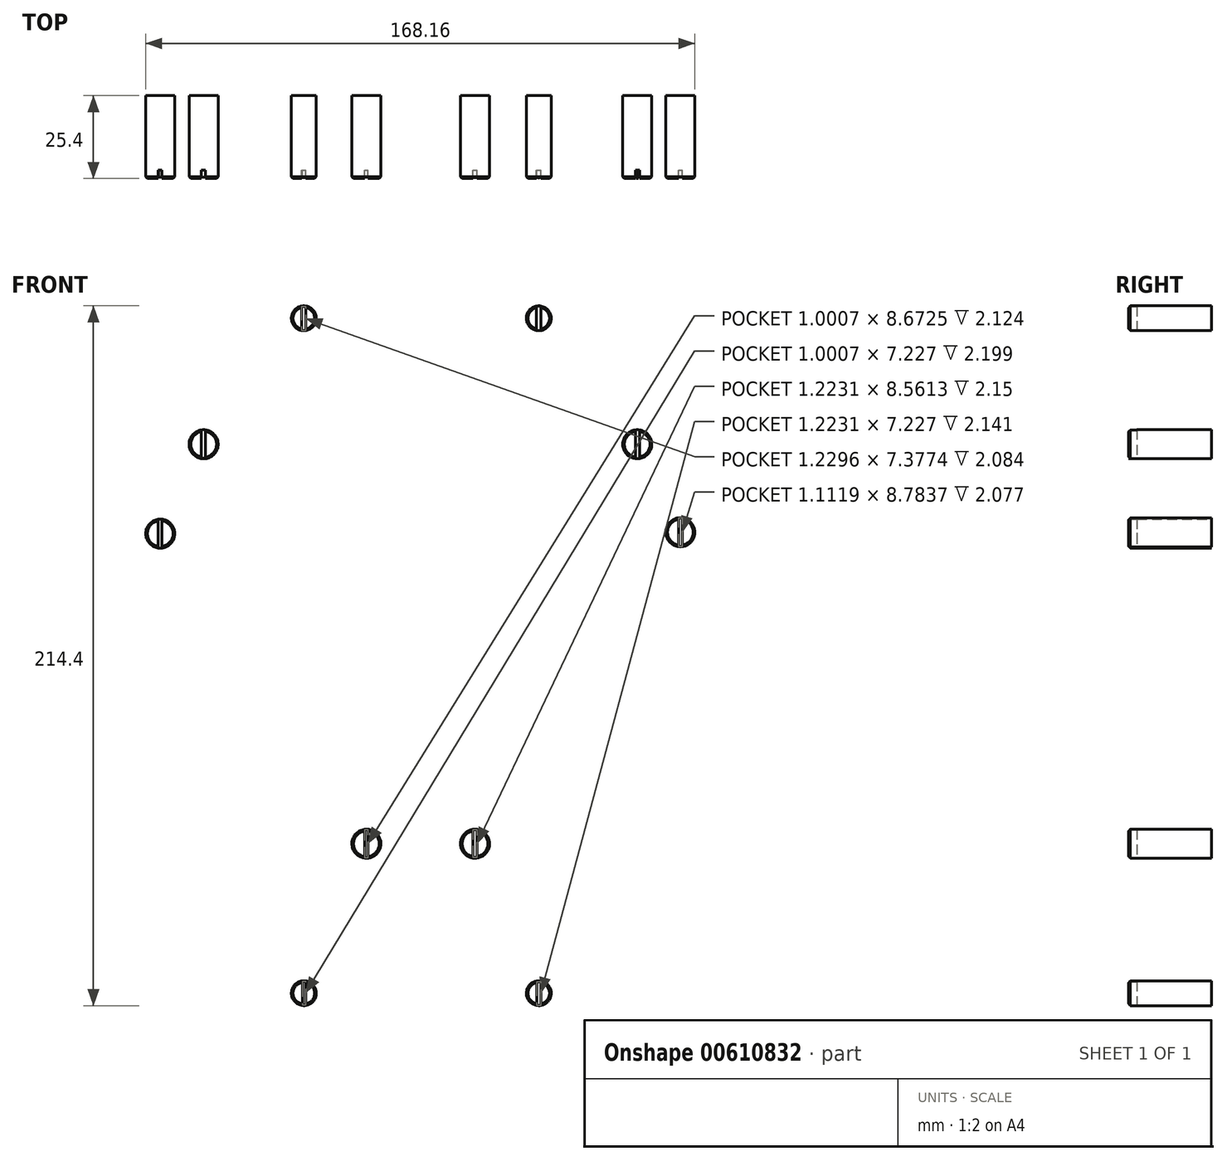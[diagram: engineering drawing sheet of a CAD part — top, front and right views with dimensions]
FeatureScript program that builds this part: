
annotation { "Feature Type Name" : "Feature", "Feature Type Description" : "" }
export const myFeature = defineFeature(function(context is Context, id is Id, definition is map)
    precondition{}
    {
        {
            var Q0;
            Q0=qCreatedBy(makeId("Front.planeOp"),FACE);
            var sketch = newSketch(context, id + "F0", { "sketchPlane" : qUnion([Q0])});
            skCircle(sketch, "E0", {"center": v(-35.62, -111.7) * mm, "radius": 3.81 * mm});
            skLineSegment(sketch, "E1", {"start": v(-43.7, -111.95) * mm, "end": v(-35.62, -111.7) * mm});
            skLineSegment(sketch, "E2", {"start": v(44.41, -111.7) * mm, "end": v(36.33, -111.7) * mm});
            skCircle(sketch, "E3", {"center": v(36.33, -111.7) * mm, "radius": 3.81 * mm});
            skCircle(sketch, "E4", {"center": v(-35.62, 95.09) * mm, "radius": 3.81 * mm});
            skCircle(sketch, "E5", {"center": v(36.33, 95.09) * mm, "radius": 3.81 * mm});
            skSolve(sketch);
        }
        {
            var Q0;
            Q0=qCreatedBy(makeId("Front.planeOp"),FACE);
            var sketch = newSketch(context, id + "F1", { "sketchPlane" : qUnion([Q0])});
            skCircle(sketch, "E6.0", {"center": v(-66.32, 56.49) * mm, "radius": 4.45 * mm});
            skCircle(sketch, "E7.0", {"center": v(-79.6, 29.11) * mm, "radius": 4.45 * mm});
            skCircle(sketch, "E8.0", {"center": v(-16.47, -65.9) * mm, "radius": 4.45 * mm});
            skCircle(sketch, "E9.0", {"center": v(16.8, -65.9) * mm, "radius": 4.45 * mm});
            skCircle(sketch, "E10.0", {"center": v(66.48, 56.49) * mm, "radius": 4.45 * mm});
            skCircle(sketch, "E11.0", {"center": v(79.66, 29.54) * mm, "radius": 4.45 * mm});
            skSolve(sketch);
        }
        {
            var Q0;
            Q0=makeQuery(id+"F0.imprint","IMPRINT",FACE,{"disambiguationData":[TD([[makeQuery(id+"F0.imprint","IMPRINT",EDGE,{"derivedFrom":sQuery(id+"F0.wireOp",EDGE,"E0")}),1.0]])]});
            var Q1;
            Q1=makeQuery(id+"F0.imprint","IMPRINT",FACE,{"disambiguationData":[TD([[makeQuery(id+"F0.imprint","IMPRINT",EDGE,{"derivedFrom":sQuery(id+"F0.wireOp",EDGE,"E3")}),1.0]])]});
            var Q2;
            Q2=makeQuery(id+"F1.imprint","IMPRINT",FACE,{"disambiguationData":[TD([[makeQuery(id+"F1.imprint","IMPRINT",EDGE,{"derivedFrom":sQuery(id+"F1.wireOp",EDGE,"E9.0")}),1.0]])]});
            var Q3;
            Q3=makeQuery(id+"F1.imprint","IMPRINT",FACE,{"disambiguationData":[TD([[makeQuery(id+"F1.imprint","IMPRINT",EDGE,{"derivedFrom":sQuery(id+"F1.wireOp",EDGE,"E8.0")}),1.0]])]});
            var Q4;
            Q4=makeQuery(id+"F1.imprint","IMPRINT",FACE,{"disambiguationData":[TD([[makeQuery(id+"F1.imprint","IMPRINT",EDGE,{"derivedFrom":sQuery(id+"F1.wireOp",EDGE,"E7.0")}),1.0]])]});
            var Q5;
            Q5=makeQuery(id+"F1.imprint","IMPRINT",FACE,{"disambiguationData":[TD([[makeQuery(id+"F1.imprint","IMPRINT",EDGE,{"derivedFrom":sQuery(id+"F1.wireOp",EDGE,"E6.0")}),1.0]])]});
            var Q6;
            Q6=makeQuery(id+"F0.imprint","IMPRINT",FACE,{"disambiguationData":[TD([[makeQuery(id+"F0.imprint","IMPRINT",EDGE,{"derivedFrom":sQuery(id+"F0.wireOp",EDGE,"E4")}),1.0]])]});
            var Q7;
            Q7=makeQuery(id+"F0.imprint","IMPRINT",FACE,{"disambiguationData":[TD([[makeQuery(id+"F0.imprint","IMPRINT",EDGE,{"derivedFrom":sQuery(id+"F0.wireOp",EDGE,"E5")}),1.0]])]});
            var Q8;
            Q8=makeQuery(id+"F1.imprint","IMPRINT",FACE,{"disambiguationData":[TD([[makeQuery(id+"F1.imprint","IMPRINT",EDGE,{"derivedFrom":sQuery(id+"F1.wireOp",EDGE,"E10.0")}),1.0]])]});
            var Q9;
            Q9=makeQuery(id+"F1.imprint","IMPRINT",FACE,{"disambiguationData":[TD([[makeQuery(id+"F1.imprint","IMPRINT",EDGE,{"derivedFrom":sQuery(id+"F1.wireOp",EDGE,"E11.0")}),1.0]])]});
            var Q10;
            Q10=sQuery(id+"F0.wireOp",EDGE,"E0");
            var Q11;
            Q11=sQuery(id+"F0.wireOp",EDGE,"E3");
            var Q12;
            Q12=sQuery(id+"F1.wireOp",EDGE,"E9.0");
            var Q13;
            Q13=sQuery(id+"F1.wireOp",EDGE,"E11.0");
            var Q14;
            Q14=sQuery(id+"F1.wireOp",EDGE,"E10.0");
            var Q15;
            Q15=sQuery(id+"F0.wireOp",EDGE,"E5");
            var Q16;
            Q16=sQuery(id+"F0.wireOp",EDGE,"E4");
            var Q17;
            Q17=sQuery(id+"F1.wireOp",EDGE,"E6.0");
            var Q18;
            Q18=sQuery(id+"F1.wireOp",EDGE,"E7.0");
            var Q19;
            Q19=sQuery(id+"F1.wireOp",EDGE,"E8.0");
            extrude(context, id + "F2", {"entities" : qUnion([Q0, Q1, Q2, Q3, Q4, Q5, Q6, Q7, Q8, Q9]), "surfaceEntities" : qUnion([Q10, Q11, Q12, Q13, Q14, Q15, Q16, Q17, Q18, Q19]), "depth" : 25.4 * mm, "offsetDistance" : 25.4 * mm});
        }
        {
            var Q0;
            Q0=qCreatedBy(makeId("Front.planeOp"),FACE);
            var sketch = newSketch(context, id + "F3", { "sketchPlane" : qUnion([Q0])});
            skLineSegment(sketch, "E12.bottom", {"start": v(-67, 61.06) * mm, "end": v(-65.77, 61.06) * mm});
            skLineSegment(sketch, "E12.top", {"start": v(-67, 52.17) * mm, "end": v(-65.77, 52.17) * mm});
            skLineSegment(sketch, "E12.left", {"start": v(-67, 61.06) * mm, "end": v(-67, 52.17) * mm});
            skLineSegment(sketch, "E12.right", {"start": v(-65.77, 61.06) * mm, "end": v(-65.77, 52.17) * mm});
            skLineSegment(sketch, "E13.bottom", {"start": v(-80.22, 33.6) * mm, "end": v(-79.11, 33.6) * mm});
            skLineSegment(sketch, "E13.top", {"start": v(-80.22, 24.7) * mm, "end": v(-79.11, 24.7) * mm});
            skLineSegment(sketch, "E13.left", {"start": v(-80.22, 33.6) * mm, "end": v(-80.22, 24.7) * mm});
            skLineSegment(sketch, "E13.right", {"start": v(-79.11, 33.6) * mm, "end": v(-79.11, 24.7) * mm});
            skLineSegment(sketch, "E14.bottom", {"start": v(65.88, 60.95) * mm, "end": v(67.2, 60.95) * mm});
            skLineSegment(sketch, "E14.top", {"start": v(65.88, 52.05) * mm, "end": v(67.2, 52.05) * mm});
            skLineSegment(sketch, "E14.left", {"start": v(65.88, 60.95) * mm, "end": v(65.88, 52.05) * mm});
            skLineSegment(sketch, "E14.right", {"start": v(67.2, 60.95) * mm, "end": v(67.2, 52.05) * mm});
            skLineSegment(sketch, "E15.bottom", {"start": v(79.1, 33.93) * mm, "end": v(80.22, 33.93) * mm});
            skLineSegment(sketch, "E15.top", {"start": v(79.1, 25.15) * mm, "end": v(80.22, 25.15) * mm});
            skLineSegment(sketch, "E15.left", {"start": v(79.1, 33.93) * mm, "end": v(79.1, 25.15) * mm});
            skLineSegment(sketch, "E15.right", {"start": v(80.22, 33.93) * mm, "end": v(80.22, 25.15) * mm});
            skLineSegment(sketch, "E16.bottom", {"start": v(16.18, -61.58) * mm, "end": v(17.4, -61.58) * mm});
            skLineSegment(sketch, "E16.top", {"start": v(16.18, -70.14) * mm, "end": v(17.4, -70.14) * mm});
            skLineSegment(sketch, "E16.left", {"start": v(16.18, -61.58) * mm, "end": v(16.18, -70.14) * mm});
            skLineSegment(sketch, "E16.right", {"start": v(17.4, -61.58) * mm, "end": v(17.4, -70.14) * mm});
            skLineSegment(sketch, "E17.bottom", {"start": v(-16.96, -61.58) * mm, "end": v(-15.96, -61.58) * mm});
            skLineSegment(sketch, "E17.top", {"start": v(-16.96, -70.25) * mm, "end": v(-15.96, -70.25) * mm});
            skLineSegment(sketch, "E17.left", {"start": v(-16.96, -61.58) * mm, "end": v(-16.96, -70.25) * mm});
            skLineSegment(sketch, "E17.right", {"start": v(-15.96, -61.58) * mm, "end": v(-15.96, -70.25) * mm});
            skLineSegment(sketch, "E18.bottom", {"start": v(-36.08, -108.05) * mm, "end": v(-35.08, -108.05) * mm});
            skLineSegment(sketch, "E18.top", {"start": v(-36.08, -115.28) * mm, "end": v(-35.08, -115.28) * mm});
            skLineSegment(sketch, "E18.left", {"start": v(-36.08, -108.05) * mm, "end": v(-36.08, -115.28) * mm});
            skLineSegment(sketch, "E18.right", {"start": v(-35.08, -108.05) * mm, "end": v(-35.08, -115.28) * mm});
            skLineSegment(sketch, "E19.bottom", {"start": v(35.74, -108.16) * mm, "end": v(36.97, -108.16) * mm});
            skLineSegment(sketch, "E19.top", {"start": v(35.74, -115.4) * mm, "end": v(36.97, -115.4) * mm});
            skLineSegment(sketch, "E19.left", {"start": v(35.74, -108.16) * mm, "end": v(35.74, -115.4) * mm});
            skLineSegment(sketch, "E19.right", {"start": v(36.97, -108.16) * mm, "end": v(36.97, -115.4) * mm});
            skLineSegment(sketch, "E20.bottom", {"start": v(-36.26, 98.7) * mm, "end": v(-35.03, 98.7) * mm});
            skLineSegment(sketch, "E20.top", {"start": v(-36.26, 91.33) * mm, "end": v(-35.03, 91.33) * mm});
            skLineSegment(sketch, "E20.left", {"start": v(-36.26, 98.7) * mm, "end": v(-36.26, 91.33) * mm});
            skLineSegment(sketch, "E20.right", {"start": v(-35.03, 98.7) * mm, "end": v(-35.03, 91.33) * mm});
            skLineSegment(sketch, "E21.bottom", {"start": v(35.63, 98.8) * mm, "end": v(36.95, 98.8) * mm});
            skLineSegment(sketch, "E21.top", {"start": v(35.63, 91.33) * mm, "end": v(36.95, 91.33) * mm});
            skLineSegment(sketch, "E21.left", {"start": v(35.63, 98.8) * mm, "end": v(35.63, 91.33) * mm});
            skLineSegment(sketch, "E21.right", {"start": v(36.95, 98.8) * mm, "end": v(36.95, 91.33) * mm});
            skSolve(sketch);
        }
        {
            var Q0;
            Q0 = qSketchRegion(id + "F3", true);
            extrude(context, id + "F4", {"entities" : qUnion([Q0]), "operationType" : NewBodyOperationType.REMOVE, "depth" : 45.97 * mm, "offsetDistance" : 25.4 * mm, "hasSecondDirection" : true, "secondDirectionOppositeDirection" : false, "secondDirectionDepth" : 22.86 * mm});
        }
        {
            var Q0;
            Q0=makeQuery(id+"F2.opExtrude","CAP_EDGE",EDGE,{"disambiguationData":[OSD([sQuery(id+"F1.wireOp",EDGE,"E6.0")])],"isStart":false});
            var Q1;
            {var subQ0=sQuery(id+"F1.wireOp",EDGE,"E7.0");Q1=makeQuery(id+"F4.boolean.opBoolean","SPLIT",EDGE,{"disambiguationData":[TD([makeQuery(id+"F4.opExtrude","SWEPT_FACE",FACE,{"disambiguationData":[OSD([sQuery(id+"F3.wireOp",EDGE,"E13.top")])]})])],"derivedFrom":makeQuery(id+"F2.opExtrude","CAP_EDGE",EDGE,{"disambiguationData":[OSD([subQ0])],"isStart":false})});}
            var Q2;
            {var subQ0=sQuery(id+"F1.wireOp",EDGE,"E7.0");Q2=makeQuery(id+"F4.boolean.opBoolean","SPLIT",EDGE,{"disambiguationData":[TD([makeQuery(id+"F4.opExtrude","SWEPT_FACE",FACE,{"disambiguationData":[OSD([sQuery(id+"F3.wireOp",EDGE,"E13.left")])]})])],"derivedFrom":makeQuery(id+"F2.opExtrude","CAP_EDGE",EDGE,{"disambiguationData":[OSD([subQ0])],"isStart":false})});}
            var Q3;
            Q3=makeQuery(id+"F2.opExtrude","CAP_EDGE",EDGE,{"disambiguationData":[OSD([sQuery(id+"F0.wireOp",EDGE,"E4")])],"isStart":false});
            var Q4;
            Q4=makeQuery(id+"F2.opExtrude","CAP_EDGE",EDGE,{"disambiguationData":[OSD([sQuery(id+"F0.wireOp",EDGE,"E5")])],"isStart":false});
            var Q5;
            {var subQ0=sQuery(id+"F1.wireOp",EDGE,"E10.0");Q5=makeQuery(id+"F4.boolean.opBoolean","SPLIT",EDGE,{"disambiguationData":[TD([makeQuery(id+"F4.opExtrude","SWEPT_FACE",FACE,{"disambiguationData":[OSD([sQuery(id+"F3.wireOp",EDGE,"E14.right")])]})])],"derivedFrom":makeQuery(id+"F2.opExtrude","CAP_EDGE",EDGE,{"disambiguationData":[OSD([subQ0])],"isStart":false})});}
            var Q6;
            {var subQ0=sQuery(id+"F1.wireOp",EDGE,"E10.0");Q6=makeQuery(id+"F4.boolean.opBoolean","SPLIT",EDGE,{"disambiguationData":[TD([makeQuery(id+"F4.opExtrude","SWEPT_FACE",FACE,{"disambiguationData":[OSD([sQuery(id+"F3.wireOp",EDGE,"E14.left")])]})])],"derivedFrom":makeQuery(id+"F2.opExtrude","CAP_EDGE",EDGE,{"disambiguationData":[OSD([subQ0])],"isStart":false})});}
            var Q7;
            Q7=makeQuery(id+"F2.opExtrude","CAP_EDGE",EDGE,{"disambiguationData":[OSD([sQuery(id+"F1.wireOp",EDGE,"E11.0")])],"isStart":false});
            var Q8;
            Q8=makeQuery(id+"F2.opExtrude","CAP_EDGE",EDGE,{"disambiguationData":[OSD([sQuery(id+"F1.wireOp",EDGE,"E9.0")])],"isStart":false});
            var Q9;
            Q9=makeQuery(id+"F2.opExtrude","CAP_EDGE",EDGE,{"disambiguationData":[OSD([sQuery(id+"F1.wireOp",EDGE,"E8.0")])],"isStart":false});
            var Q10;
            Q10=makeQuery(id+"F2.opExtrude","CAP_EDGE",EDGE,{"disambiguationData":[OSD([sQuery(id+"F0.wireOp",EDGE,"E0")])],"isStart":false});
            var Q11;
            Q11=makeQuery(id+"F2.opExtrude","CAP_EDGE",EDGE,{"disambiguationData":[OSD([sQuery(id+"F0.wireOp",EDGE,"E3")])],"isStart":false});
            chamfer(context, id + "F5", {"entities" : qUnion([Q0, Q1, Q2, Q3, Q4, Q5, Q6, Q7, Q8, Q9, Q10, Q11]), "width" : 0.5 * mm, "tangentPropagation" : true});
        }
    });
